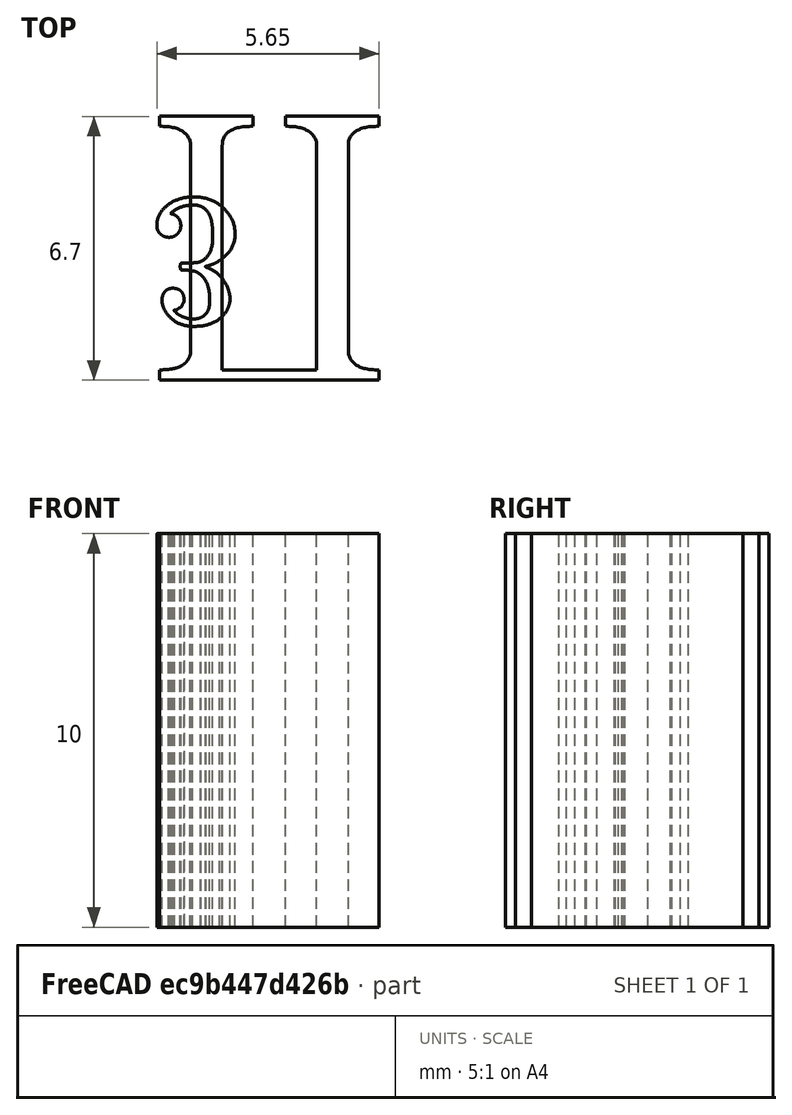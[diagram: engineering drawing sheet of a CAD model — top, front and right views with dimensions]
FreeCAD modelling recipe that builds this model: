
FCSTD DOCUMENT  (FreeCAD 0.19R)
Label: 6_product
License: All rights reserved
LicenseURL: http://en.wikipedia.org/wiki/All_rights_reserved
objects: Part::Feature×6, Sketcher::SketchObject×2, PartDesign::Pad×2, PartDesign::Body×2
note: 14 computed .brp shape members not serialized (recipe doc carries the construction recipe); baked Part::Feature solids carry a one-line shape summary decoded from their .brp

FEATURE [Part::Feature] MJX_10_TEX_LO_220F
  shape: bbox 5.579 x 6.704 x 2e-07 mm, 0 faces, 0 solids (baked)
FEATURE [Part::Feature] MJX_10_TEX_I_6B
  shape: bbox 2.179 x 3.376 x 2e-07 mm, 0 faces, 0 solids (baked)
FEATURE [Part::Feature] MJX_10_TEX_N_3D
  shape: bbox 3.189 x 0.1915 x 2e-07 mm, 0 faces, 0 solids (baked)
FEATURE [Part::Feature] MJX_10_TEX_N_3D001
  shape: bbox 3.189 x 0.1915 x 2e-07 mm, 0 faces, 0 solids (baked)
FEATURE [Part::Feature] MJX_10_TEX_N_31
  shape: bbox 1.647 x 3.189 x 2e-07 mm, 0 faces, 0 solids (baked)
FEATURE [Part::Feature] MJX_10_TEX_N_33
  shape: bbox 1.987 x 3.29 x 2e-07 mm, 0 faces, 0 solids (baked)
FEATURE [Sketcher::SketchObject] Sketch
  FullyConstrained = false
  MapMode = 5
  Support = -> [XY_Plane]
  sketch-geometry (37):
    g0: BSplineCurve PolesCount=3 KnotsCount=2 Degree=2 IsPeriodic=0
    g1: BSplineCurve PolesCount=3 KnotsCount=2 Degree=2 IsPeriodic=0
    g2: BSplineCurve PolesCount=3 KnotsCount=2 Degree=2 IsPeriodic=0
    g3: BSplineCurve PolesCount=3 KnotsCount=2 Degree=2 IsPeriodic=0
    g4: BSplineCurve PolesCount=3 KnotsCount=2 Degree=2 IsPeriodic=0
    g5: BSplineCurve PolesCount=3 KnotsCount=2 Degree=2 IsPeriodic=0
    g6: BSplineCurve PolesCount=3 KnotsCount=2 Degree=2 IsPeriodic=0
    g7: BSplineCurve PolesCount=3 KnotsCount=2 Degree=2 IsPeriodic=0
    g8: BSplineCurve PolesCount=3 KnotsCount=2 Degree=2 IsPeriodic=0
    g9: BSplineCurve PolesCount=2 KnotsCount=2 Degree=1 IsPeriodic=0
    g10: BSplineCurve PolesCount=2 KnotsCount=2 Degree=1 IsPeriodic=0
    g11: BSplineCurve PolesCount=2 KnotsCount=2 Degree=1 IsPeriodic=0
    g12: BSplineCurve PolesCount=2 KnotsCount=2 Degree=1 IsPeriodic=0
    g13: BSplineCurve PolesCount=2 KnotsCount=2 Degree=1 IsPeriodic=0
    g14: BSplineCurve PolesCount=3 KnotsCount=2 Degree=2 IsPeriodic=0
    g15: BSplineCurve PolesCount=2 KnotsCount=2 Degree=1 IsPeriodic=0
    g16: BSplineCurve PolesCount=3 KnotsCount=2 Degree=2 IsPeriodic=0
    g17: BSplineCurve PolesCount=2 KnotsCount=2 Degree=1 IsPeriodic=0
    g18: BSplineCurve PolesCount=2 KnotsCount=2 Degree=1 IsPeriodic=0
    g19: BSplineCurve PolesCount=2 KnotsCount=2 Degree=1 IsPeriodic=0
    g20: BSplineCurve PolesCount=2 KnotsCount=2 Degree=1 IsPeriodic=0
    g21: BSplineCurve PolesCount=2 KnotsCount=2 Degree=1 IsPeriodic=0
    g22: BSplineCurve PolesCount=3 KnotsCount=2 Degree=2 IsPeriodic=0
    g23: BSplineCurve PolesCount=3 KnotsCount=2 Degree=2 IsPeriodic=0
    g24: BSplineCurve PolesCount=2 KnotsCount=2 Degree=1 IsPeriodic=0
    g25: BSplineCurve PolesCount=2 KnotsCount=2 Degree=1 IsPeriodic=0
    g26: BSplineCurve PolesCount=2 KnotsCount=2 Degree=1 IsPeriodic=0
    g27: BSplineCurve PolesCount=2 KnotsCount=2 Degree=1 IsPeriodic=0
    g28: BSplineCurve PolesCount=3 KnotsCount=2 Degree=2 IsPeriodic=0
    g29: BSplineCurve PolesCount=2 KnotsCount=2 Degree=1 IsPeriodic=0
    g30: BSplineCurve PolesCount=2 KnotsCount=2 Degree=1 IsPeriodic=0
    g31: BSplineCurve PolesCount=2 KnotsCount=2 Degree=1 IsPeriodic=0
    g32: BSplineCurve PolesCount=2 KnotsCount=2 Degree=1 IsPeriodic=0
    g33: BSplineCurve PolesCount=2 KnotsCount=2 Degree=1 IsPeriodic=0
    g34: BSplineCurve PolesCount=3 KnotsCount=2 Degree=2 IsPeriodic=0
    g35: BSplineCurve PolesCount=3 KnotsCount=2 Degree=2 IsPeriodic=0
    g36: BSplineCurve PolesCount=2 KnotsCount=2 Degree=1 IsPeriodic=0
  constraints (37):
    c: Coincident(g0,g1)
    c: Coincident(g1,g2)
    c: Coincident(g2,g3)
    c: Coincident(g3,g4)
    c: Coincident(g4,g5)
    c: Coincident(g5,g6)
    c: Coincident(g6,g7)
    c: Coincident(g7,g8)
    c: Coincident(g8,g9)
    c: Coincident(g9,g10)
    c: Coincident(g10,g11)
    c: Coincident(g11,g12)
    c: Coincident(g12,g13)
    c: Coincident(g13,g14)
    c: Coincident(g14,g15)
    c: Coincident(g15,g16)
    c: Coincident(g16,g17)
    c: Coincident(g17,g18)
    c: Coincident(g18,g19)
    c: Coincident(g19,g20)
    c: Coincident(g20,g21)
    c: Coincident(g21,g22)
    c: Coincident(g22,g23)
    c: Coincident(g23,g24)
    c: Coincident(g24,g25)
    c: Coincident(g25,g26)
    c: Coincident(g26,g27)
    c: Coincident(g27,g28)
    c: Coincident(g28,g29)
    c: Coincident(g29,g30)
    c: Coincident(g30,g31)
    c: Coincident(g31,g32)
    c: Coincident(g32,g33)
    c: Coincident(g33,g34)
    c: Coincident(g34,g35)
    c: Coincident(g35,g36)
    c: Coincident(g36,g0)
FEATURE [Sketcher::SketchObject] Sketch001
  FullyConstrained = false
  MapMode = 5
  Support = -> [XY_Plane001]
  sketch-geometry (57):
    g0: BSplineCurve PolesCount=3 KnotsCount=2 Degree=2 IsPeriodic=0
    g1: BSplineCurve PolesCount=3 KnotsCount=2 Degree=2 IsPeriodic=0
    g2: BSplineCurve PolesCount=3 KnotsCount=2 Degree=2 IsPeriodic=0
    g3: BSplineCurve PolesCount=3 KnotsCount=2 Degree=2 IsPeriodic=0
    g4: BSplineCurve PolesCount=3 KnotsCount=2 Degree=2 IsPeriodic=0
    g5: BSplineCurve PolesCount=3 KnotsCount=2 Degree=2 IsPeriodic=0
    g6: BSplineCurve PolesCount=3 KnotsCount=2 Degree=2 IsPeriodic=0
    g7: BSplineCurve PolesCount=3 KnotsCount=2 Degree=2 IsPeriodic=0
    g8: BSplineCurve PolesCount=3 KnotsCount=2 Degree=2 IsPeriodic=0
    g9: BSplineCurve PolesCount=2 KnotsCount=2 Degree=1 IsPeriodic=0
    g10: BSplineCurve PolesCount=3 KnotsCount=2 Degree=2 IsPeriodic=0
    g11: BSplineCurve PolesCount=3 KnotsCount=2 Degree=2 IsPeriodic=0
    g12: BSplineCurve PolesCount=3 KnotsCount=2 Degree=2 IsPeriodic=0
    g13: BSplineCurve PolesCount=3 KnotsCount=2 Degree=2 IsPeriodic=0
    g14: BSplineCurve PolesCount=3 KnotsCount=2 Degree=2 IsPeriodic=0
    g15: BSplineCurve PolesCount=3 KnotsCount=2 Degree=2 IsPeriodic=0
    g16: BSplineCurve PolesCount=3 KnotsCount=2 Degree=2 IsPeriodic=0
    g17: BSplineCurve PolesCount=3 KnotsCount=2 Degree=2 IsPeriodic=0
    g18: BSplineCurve PolesCount=3 KnotsCount=2 Degree=2 IsPeriodic=0
    g19: BSplineCurve PolesCount=3 KnotsCount=2 Degree=2 IsPeriodic=0
    g20: BSplineCurve PolesCount=3 KnotsCount=2 Degree=2 IsPeriodic=0
    g21: BSplineCurve PolesCount=3 KnotsCount=2 Degree=2 IsPeriodic=0
    g22: BSplineCurve PolesCount=3 KnotsCount=2 Degree=2 IsPeriodic=0
    g23: BSplineCurve PolesCount=3 KnotsCount=2 Degree=2 IsPeriodic=0
    g24: BSplineCurve PolesCount=3 KnotsCount=2 Degree=2 IsPeriodic=0
    g25: BSplineCurve PolesCount=3 KnotsCount=2 Degree=2 IsPeriodic=0
    g26: BSplineCurve PolesCount=3 KnotsCount=2 Degree=2 IsPeriodic=0
    g27: BSplineCurve PolesCount=3 KnotsCount=2 Degree=2 IsPeriodic=0
    g28: BSplineCurve PolesCount=2 KnotsCount=2 Degree=1 IsPeriodic=0
    g29: BSplineCurve PolesCount=3 KnotsCount=2 Degree=2 IsPeriodic=0
    g30: BSplineCurve PolesCount=3 KnotsCount=2 Degree=2 IsPeriodic=0
    g31: BSplineCurve PolesCount=3 KnotsCount=2 Degree=2 IsPeriodic=0
    g32: BSplineCurve PolesCount=2 KnotsCount=2 Degree=1 IsPeriodic=0
    g33: BSplineCurve PolesCount=3 KnotsCount=2 Degree=2 IsPeriodic=0
    g34: BSplineCurve PolesCount=3 KnotsCount=2 Degree=2 IsPeriodic=0
    g35: BSplineCurve PolesCount=2 KnotsCount=2 Degree=1 IsPeriodic=0
    g36: BSplineCurve PolesCount=2 KnotsCount=2 Degree=1 IsPeriodic=0
    g37: BSplineCurve PolesCount=3 KnotsCount=2 Degree=2 IsPeriodic=0
    g38: BSplineCurve PolesCount=3 KnotsCount=2 Degree=2 IsPeriodic=0
    g39: BSplineCurve PolesCount=3 KnotsCount=2 Degree=2 IsPeriodic=0
    g40: BSplineCurve PolesCount=3 KnotsCount=2 Degree=2 IsPeriodic=0
    g41: BSplineCurve PolesCount=3 KnotsCount=2 Degree=2 IsPeriodic=0
    g42: BSplineCurve PolesCount=2 KnotsCount=2 Degree=1 IsPeriodic=0
    g43: BSplineCurve PolesCount=3 KnotsCount=2 Degree=2 IsPeriodic=0
    g44: BSplineCurve PolesCount=3 KnotsCount=2 Degree=2 IsPeriodic=0
    g45: BSplineCurve PolesCount=3 KnotsCount=2 Degree=2 IsPeriodic=0
    g46: BSplineCurve PolesCount=3 KnotsCount=2 Degree=2 IsPeriodic=0
    g47: BSplineCurve PolesCount=3 KnotsCount=2 Degree=2 IsPeriodic=0
    g48: BSplineCurve PolesCount=2 KnotsCount=2 Degree=1 IsPeriodic=0
    g49: BSplineCurve PolesCount=3 KnotsCount=2 Degree=2 IsPeriodic=0
    g50: BSplineCurve PolesCount=3 KnotsCount=2 Degree=2 IsPeriodic=0
    g51: BSplineCurve PolesCount=3 KnotsCount=2 Degree=2 IsPeriodic=0
    g52: BSplineCurve PolesCount=3 KnotsCount=2 Degree=2 IsPeriodic=0
    g53: BSplineCurve PolesCount=3 KnotsCount=2 Degree=2 IsPeriodic=0
    g54: BSplineCurve PolesCount=3 KnotsCount=2 Degree=2 IsPeriodic=0
    g55: BSplineCurve PolesCount=3 KnotsCount=2 Degree=2 IsPeriodic=0
    g56: BSplineCurve PolesCount=3 KnotsCount=2 Degree=2 IsPeriodic=0
  constraints (57):
    c: Coincident(g0,g1)
    c: Coincident(g1,g2)
    c: Coincident(g2,g3)
    c: Coincident(g3,g4)
    c: Coincident(g4,g5)
    c: Coincident(g5,g6)
    c: Coincident(g6,g7)
    c: Coincident(g7,g8)
    c: Coincident(g8,g9)
    c: Coincident(g9,g10)
    c: Coincident(g10,g11)
    c: Coincident(g11,g12)
    c: Coincident(g12,g13)
    c: Coincident(g13,g14)
    c: Coincident(g14,g15)
    c: Coincident(g15,g16)
    c: Coincident(g16,g17)
    c: Coincident(g17,g18)
    c: Coincident(g18,g19)
    c: Coincident(g19,g20)
    c: Coincident(g20,g21)
    c: Coincident(g21,g22)
    c: Coincident(g22,g23)
    c: Coincident(g23,g24)
    c: Coincident(g24,g25)
    c: Coincident(g25,g26)
    c: Coincident(g26,g27)
    c: Coincident(g27,g28)
    c: Coincident(g28,g29)
    c: Coincident(g29,g30)
    c: Coincident(g30,g31)
    c: Coincident(g31,g32)
    c: Coincident(g32,g33)
    c: Coincident(g33,g34)
    c: Coincident(g34,g35)
    c: Coincident(g35,g36)
    c: Coincident(g36,g37)
    c: Coincident(g37,g38)
    c: Coincident(g38,g39)
    c: Coincident(g39,g40)
    c: Coincident(g40,g41)
    c: Coincident(g41,g42)
    c: Coincident(g42,g43)
    c: Coincident(g43,g44)
    c: Coincident(g44,g45)
    c: Coincident(g45,g46)
    c: Coincident(g46,g47)
    c: Coincident(g47,g48)
    c: Coincident(g48,g49)
    c: Coincident(g49,g50)
    c: Coincident(g50,g51)
    c: Coincident(g51,g52)
    c: Coincident(g52,g53)
    c: Coincident(g53,g54)
    c: Coincident(g54,g55)
    c: Coincident(g55,g56)
    c: Coincident(g56,g0)
FEATURE [PartDesign::Pad] Pad
  Direction = (1,1,1)
  Length = 10
  Length2 = 100
  Profile = -> Sketch
  Type = 0
FEATURE [PartDesign::Body] Body
  Group = -> [Sketch,Pad]
  Origin = -> Origin
  Tip = -> Pad
FEATURE [PartDesign::Pad] Pad001
  Direction = (1,1,1)
  Length = 10
  Length2 = 100
  Profile = -> Sketch001
  Type = 0
FEATURE [PartDesign::Body] Body001
  Group = -> [Sketch001,Pad001]
  Origin = -> Origin001
  Tip = -> Pad001
